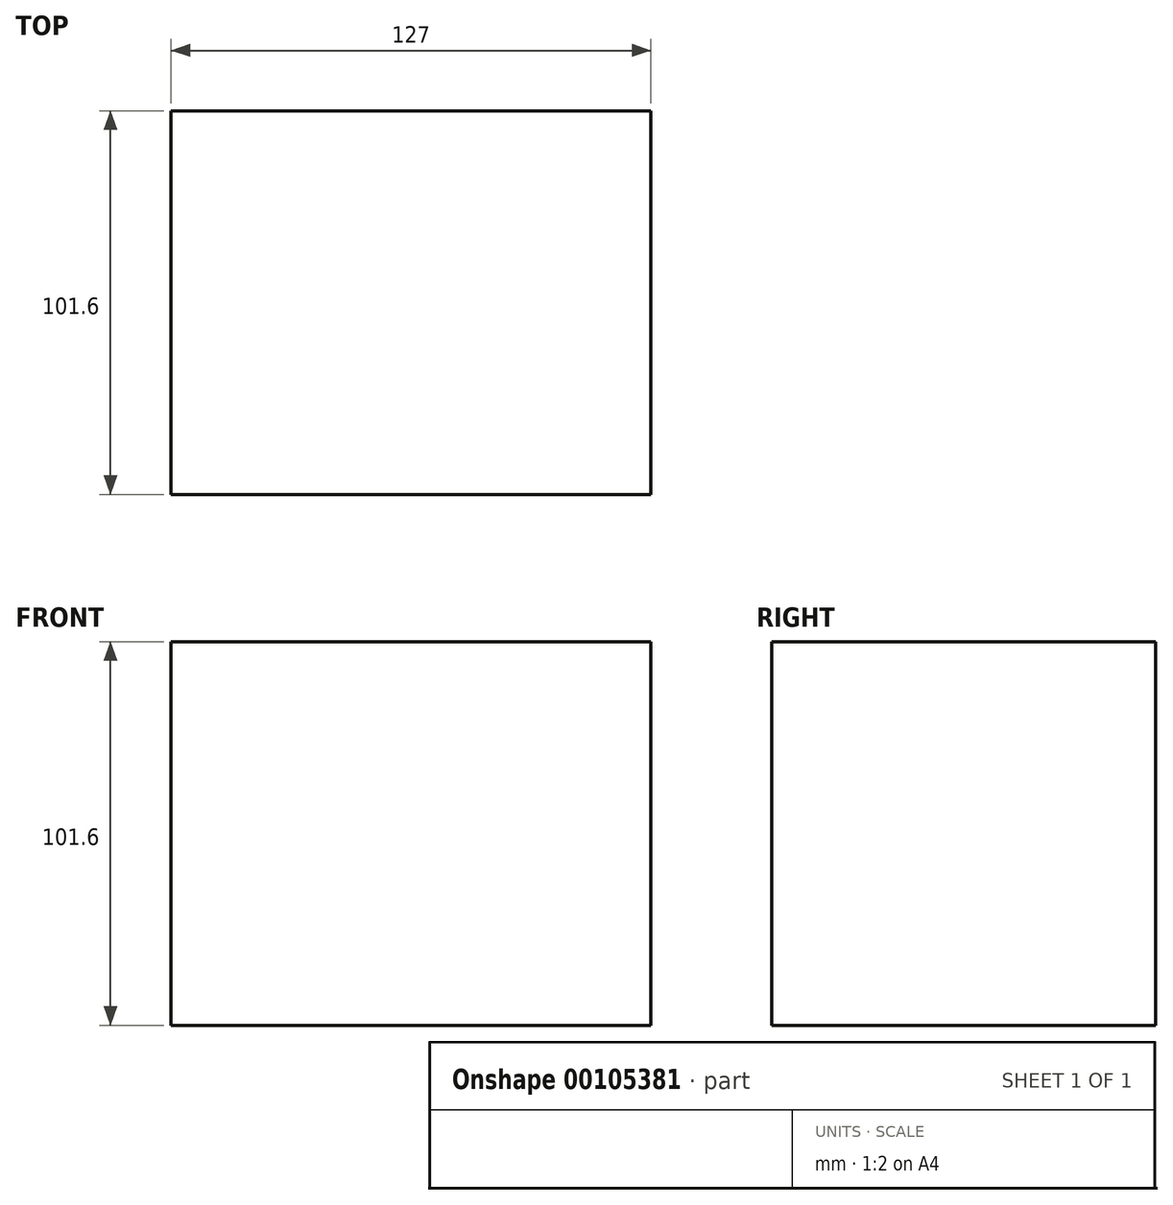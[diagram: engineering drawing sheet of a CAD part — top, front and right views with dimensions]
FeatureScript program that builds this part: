
annotation { "Feature Type Name" : "Feature", "Feature Type Description" : "" }
export const myFeature = defineFeature(function(context is Context, id is Id, definition is map)
    precondition{}
    {
        {
            var Q0;
            Q0=qCreatedBy(makeId("Top.planeOp"),FACE);
            var sketch = newSketch(context, id + "F0", { "sketchPlane" : qUnion([Q0])});
            skLineSegment(sketch, "E0.bottom", {"start": v(-45.58, 47.9) * mm, "end": v(81.42, 47.9) * mm});
            skLineSegment(sketch, "E0.top", {"start": v(-45.58, -53.7) * mm, "end": v(81.42, -53.7) * mm});
            skLineSegment(sketch, "E0.left", {"start": v(-45.58, 47.9) * mm, "end": v(-45.58, -53.7) * mm});
            skLineSegment(sketch, "E0.right", {"start": v(81.42, 47.9) * mm, "end": v(81.42, -53.7) * mm});
            skSolve(sketch);
        }
        {
            var Q0;
            Q0 = qSketchRegion(id + "F0", true);
            extrude(context, id + "F1", {"entities" : qUnion([Q0]), "depth" : 101.6 * mm});
        }
    });
